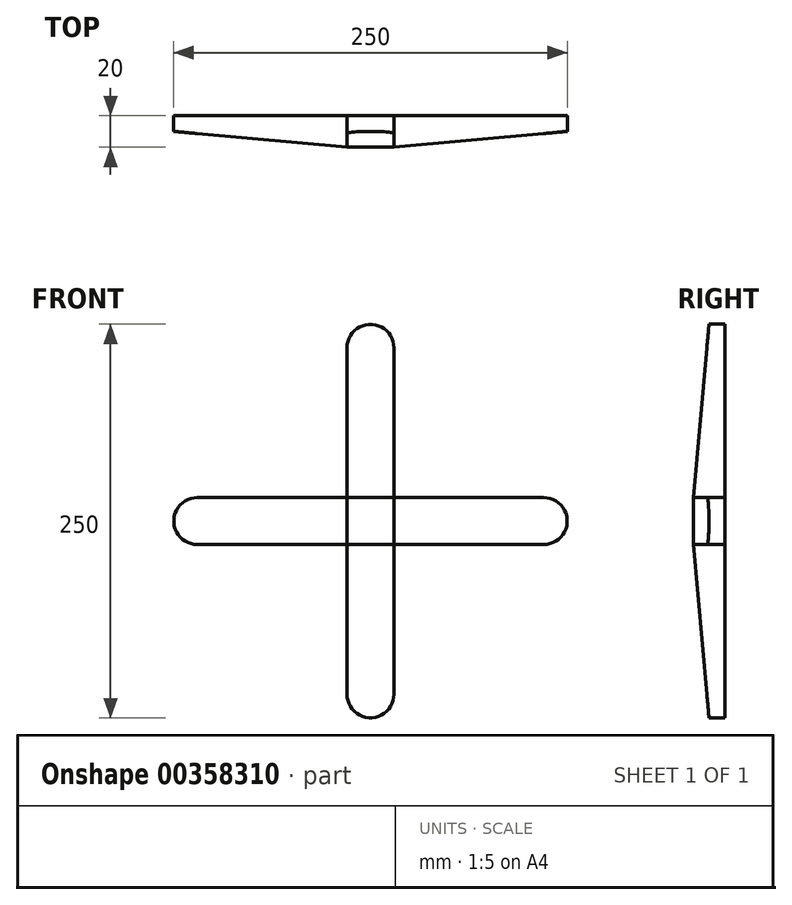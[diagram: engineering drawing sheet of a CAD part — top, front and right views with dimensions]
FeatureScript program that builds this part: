
annotation { "Feature Type Name" : "Feature", "Feature Type Description" : "" }
export const myFeature = defineFeature(function(context is Context, id is Id, definition is map)
    precondition{}
    {
        {
            var Q0;
            Q0=qCreatedBy(makeId("Front.planeOp"),FACE);
            var sketch = newSketch(context, id + "F0", { "sketchPlane" : qUnion([Q0])});
            skLineSegment(sketch, "E0.bottom", {"start": v(15, -15) * mm, "end": v(-15, -15) * mm});
            skLineSegment(sketch, "E0.top", {"start": v(15, 15) * mm, "end": v(-15, 15) * mm});
            skLineSegment(sketch, "E0.left", {"start": v(15, -15) * mm, "end": v(15, 15) * mm});
            skLineSegment(sketch, "E0.right", {"start": v(-15, -15) * mm, "end": v(-15, 15) * mm});
            skPoint(sketch, "E0.middle", {"position": v(0, 0) * mm});
            skSolve(sketch);
        }
        {
            var Q0;
            Q0=makeQuery(id+"F0.imprint","IMPRINT",FACE,{"disambiguationData":[TD([[makeQuery(id+"F0.imprint","IMPRINT",EDGE,{"derivedFrom":sQuery(id+"F0.wireOp",EDGE,"E0.bottom")}),-1.0]])]});
            extrude(context, id + "F1", {"entities" : qUnion([Q0]), "depth" : 20 * mm});
        }
        {
            var Q0;
            Q0=makeQuery(id+"F1.opExtrude","SWEPT_FACE",FACE,{"disambiguationData":[OSD([sQuery(id+"F0.wireOp",EDGE,"E0.bottom")])]});
            var sketch = newSketch(context, id + "F2", { "sketchPlane" : qUnion([Q0])});
            skLineSegment(sketch, "E1.bottom", {"start": v(-15, 20) * mm, "end": v(15, 20) * mm});
            skLineSegment(sketch, "E1.top", {"start": v(-15, 0) * mm, "end": v(15, 0) * mm});
            skLineSegment(sketch, "E1.left", {"start": v(-15, 20) * mm, "end": v(-15, 0) * mm});
            skLineSegment(sketch, "E1.right", {"start": v(15, 20) * mm, "end": v(15, 0) * mm});
            skSolve(sketch);
        }
        {
            var Q0;
            Q0=makeQuery(id+"F1.opExtrude","SWEPT_FACE",FACE,{"disambiguationData":[OSD([sQuery(id+"F0.wireOp",EDGE,"E0.right")])]});
            var sketch = newSketch(context, id + "F3", { "sketchPlane" : qUnion([Q0])});
            skLineSegment(sketch, "E2.bottom", {"start": v(0, 15) * mm, "end": v(20, 15) * mm});
            skLineSegment(sketch, "E2.top", {"start": v(0, -15) * mm, "end": v(20, -15) * mm});
            skLineSegment(sketch, "E2.left", {"start": v(0, 15) * mm, "end": v(0, -15) * mm});
            skLineSegment(sketch, "E2.right", {"start": v(20, 15) * mm, "end": v(20, -15) * mm});
            skSolve(sketch);
        }
        {
            var Q0;
            Q0=makeQuery(id+"F1.opExtrude","SWEPT_FACE",FACE,{"disambiguationData":[OSD([sQuery(id+"F0.wireOp",EDGE,"E0.top")])]});
            var sketch = newSketch(context, id + "F4", { "sketchPlane" : qUnion([Q0])});
            skLineSegment(sketch, "E3.bottom", {"start": v(-15, 0) * mm, "end": v(15, 0) * mm});
            skLineSegment(sketch, "E3.top", {"start": v(-15, -20) * mm, "end": v(15, -20) * mm});
            skLineSegment(sketch, "E3.left", {"start": v(-15, 0) * mm, "end": v(-15, -20) * mm});
            skLineSegment(sketch, "E3.right", {"start": v(15, 0) * mm, "end": v(15, -20) * mm});
            skSolve(sketch);
        }
        {
            var Q0;
            Q0=makeQuery(id+"F1.opExtrude","SWEPT_FACE",FACE,{"disambiguationData":[OSD([sQuery(id+"F0.wireOp",EDGE,"E0.left")])]});
            var sketch = newSketch(context, id + "F5", { "sketchPlane" : qUnion([Q0])});
            skLineSegment(sketch, "E4.bottom", {"start": v(-20, 15) * mm, "end": v(0, 15) * mm});
            skLineSegment(sketch, "E4.top", {"start": v(-20, -15) * mm, "end": v(0, -15) * mm});
            skLineSegment(sketch, "E4.left", {"start": v(-20, 15) * mm, "end": v(-20, -15) * mm});
            skLineSegment(sketch, "E4.right", {"start": v(0, 15) * mm, "end": v(0, -15) * mm});
            skSolve(sketch);
        }
        {
            var Q0;
            Q0=makeQuery(id+"F5.imprint","IMPRINT",FACE,{"disambiguationData":[TD([[makeQuery(id+"F5.imprint","IMPRINT",EDGE,{"derivedFrom":sQuery(id+"F5.wireOp",EDGE,"E4.bottom")}),-1.0]])]});
            extrude(context, id + "F6", {"entities" : qUnion([Q0]), "operationType" : NewBodyOperationType.ADD, "depth" : 110 * mm});
        }
        {
            var Q0;
            Q0=makeQuery(id+"F4.imprint","IMPRINT",FACE,{"disambiguationData":[TD([[makeQuery(id+"F4.imprint","IMPRINT",EDGE,{"derivedFrom":sQuery(id+"F4.wireOp",EDGE,"E3.bottom")}),1.0]])]});
            extrude(context, id + "F7", {"entities" : qUnion([Q0]), "operationType" : NewBodyOperationType.ADD, "depth" : 110 * mm});
        }
        {
            var Q0;
            Q0=makeQuery(id+"F3.imprint","IMPRINT",FACE,{"disambiguationData":[TD([[makeQuery(id+"F3.imprint","IMPRINT",EDGE,{"derivedFrom":sQuery(id+"F3.wireOp",EDGE,"E2.bottom")}),1.0]])]});
            extrude(context, id + "F8", {"entities" : qUnion([Q0]), "operationType" : NewBodyOperationType.ADD, "depth" : 110 * mm});
        }
        {
            var Q0;
            Q0=makeQuery(id+"F2.imprint","IMPRINT",FACE,{"disambiguationData":[TD([[makeQuery(id+"F2.imprint","IMPRINT",EDGE,{"derivedFrom":sQuery(id+"F2.wireOp",EDGE,"E1.bottom")}),1.0]])]});
            extrude(context, id + "F9", {"entities" : qUnion([Q0]), "operationType" : NewBodyOperationType.ADD, "depth" : 110 * mm});
        }
        {
            var Q0;
            Q0=makeQuery(id+"F8.opExtrude","CAP_EDGE",EDGE,{"disambiguationData":[OSD([sQuery(id+"F3.wireOp",EDGE,"E2.right")])],"isStart":false});
            var Q1;
            Q1=makeQuery(id+"F9.opExtrude","CAP_EDGE",EDGE,{"disambiguationData":[OSD([sQuery(id+"F2.wireOp",EDGE,"E1.bottom")])],"isStart":false});
            var Q2;
            Q2=makeQuery(id+"F6.opExtrude","CAP_EDGE",EDGE,{"disambiguationData":[OSD([sQuery(id+"F5.wireOp",EDGE,"E4.left")])],"isStart":false});
            var Q3;
            Q3=makeQuery(id+"F7.opExtrude","CAP_EDGE",EDGE,{"disambiguationData":[OSD([sQuery(id+"F4.wireOp",EDGE,"E3.top")])],"isStart":false});
            chamfer(context, id + "F10", {"entities" : qUnion([Q0, Q1, Q2, Q3]), "chamferType" : ChamferType.TWO_OFFSETS, "width1" : 10 * mm, "oppositeDirection" : false, "width2" : 110 * mm, "tangentPropagation" : true});
        }
        {
            var Q0;
            Q0=makeQuery(id+"F7.opExtrude","CAP_EDGE",EDGE,{"disambiguationData":[OSD([sQuery(id+"F4.wireOp",EDGE,"E3.right")])],"isStart":false});
            var Q1;
            Q1=makeQuery(id+"F7.opExtrude","CAP_EDGE",EDGE,{"disambiguationData":[OSD([sQuery(id+"F4.wireOp",EDGE,"E3.left")])],"isStart":false});
            var Q2;
            Q2=makeQuery(id+"F8.opExtrude","CAP_EDGE",EDGE,{"disambiguationData":[OSD([sQuery(id+"F3.wireOp",EDGE,"E2.bottom")])],"isStart":false});
            var Q3;
            Q3=makeQuery(id+"F8.opExtrude","CAP_EDGE",EDGE,{"disambiguationData":[OSD([sQuery(id+"F3.wireOp",EDGE,"E2.top")])],"isStart":false});
            var Q4;
            Q4=makeQuery(id+"F9.opExtrude","CAP_EDGE",EDGE,{"disambiguationData":[OSD([sQuery(id+"F2.wireOp",EDGE,"E1.left")])],"isStart":false});
            var Q5;
            Q5=makeQuery(id+"F9.opExtrude","CAP_EDGE",EDGE,{"disambiguationData":[OSD([sQuery(id+"F2.wireOp",EDGE,"E1.right")])],"isStart":false});
            var Q6;
            Q6=makeQuery(id+"F6.opExtrude","CAP_EDGE",EDGE,{"disambiguationData":[OSD([sQuery(id+"F5.wireOp",EDGE,"E4.top")])],"isStart":false});
            var Q7;
            Q7=makeQuery(id+"F6.opExtrude","CAP_EDGE",EDGE,{"disambiguationData":[OSD([sQuery(id+"F5.wireOp",EDGE,"E4.bottom")])],"isStart":false});
            fillet(context, id + "F11", {"entities" : qUnion([Q0, Q1, Q2, Q3, Q4, Q5, Q6, Q7]), "radius" : 15 * mm, "tangentPropagation" : true, "allowEdgeOverflow" : false});
        }
    });
